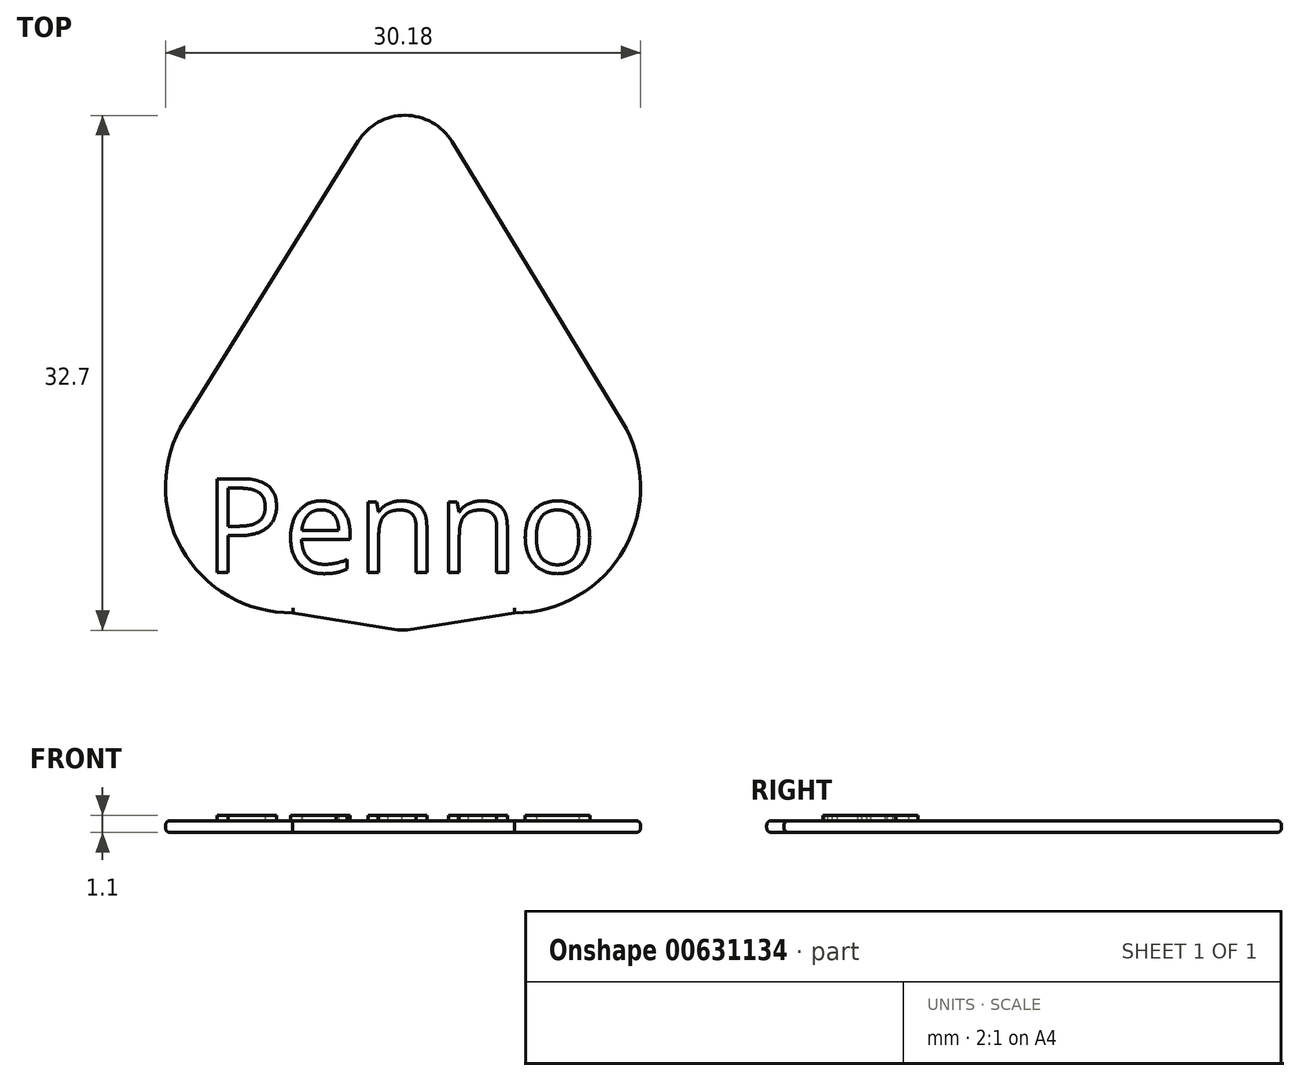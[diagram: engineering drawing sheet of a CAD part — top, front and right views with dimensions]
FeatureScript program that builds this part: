
annotation { "Feature Type Name" : "Feature", "Feature Type Description" : "" }
export const myFeature = defineFeature(function(context is Context, id is Id, definition is map)
    precondition{}
    {
        {
            var Q0;
            Q0=qCreatedBy(makeId("Top.planeOp"),FACE);
            var sketch = newSketch(context, id + "F0", { "sketchPlane" : qUnion([Q0])});
            skLineSegment(sketch, "E0", {"start": v(35.4, 12.16) * mm, "end": v(24.6, 29.92) * mm});
            skLineSegment(sketch, "E1", {"start": v(18.63, 29.95) * mm, "end": v(7.6, 12.23) * mm});
            skPoint(sketch, "E2.visualSharp", {"position": v(21.64, 34.78) * mm});
            skArc(sketch, "E2.filletArc", {"start": v(24.6, 29.92) * mm, "mid": v(21.62, 31.6) * mm, "end": v(18.63, 29.95) * mm});
            skPoint(sketch, "E3.visualSharp", {"position": v(0, 0) * mm});
            skArc(sketch, "E3.filletArc", {"start": v(7.6, 12.23) * mm, "mid": v(7.43, 4.08) * mm, "end": v(14.48, 0) * mm});
            skPoint(sketch, "E4.visualSharp", {"position": v(44.08, -2.08) * mm});
            skArc(sketch, "E4.filletArc", {"start": v(28.58, 0) * mm, "mid": v(35.55, 4.08) * mm, "end": v(35.4, 12.16) * mm});
            skLineSegment(sketch, "E5", {"start": v(7.4, -7.26) * mm, "end": v(35.4, -7.26) * mm, "construction": true});
            skPoint(sketch, "E6", {"position": v(21.47, -1.12) * mm});
            skLineSegment(sketch, "E7", {"start": v(2.06, -2.05) * mm, "end": v(2.06, 29.95) * mm, "construction": true});
            skLineSegment(sketch, "E8", {"start": v(14.48, 0) * mm, "end": v(21.15, -1.07) * mm});
            skLineSegment(sketch, "E9", {"start": v(28.58, 0) * mm, "end": v(21.78, -1.07) * mm});
            skArc(sketch, "E10.filletArc", {"start": v(21.15, -1.07) * mm, "mid": v(21.47, -1.1) * mm, "end": v(21.78, -1.07) * mm});
            skPoint(sketch, "E11", {"position": v(30, 21.04) * mm});
            skPoint(sketch, "E12", {"position": v(13.1, 21.04) * mm});
            skSolve(sketch);
        }
        {
            var Q0;
            Q0 = qSketchRegion(id + "F0", true);
            extrude(context, id + "F1", {"entities" : qUnion([Q0]), "depth" : 0.75 * mm, "offsetDistance" : 25 * mm});
        }
        {
            var Q0;
            Q0=makeQuery(id+"F1.opExtrude","CAP_EDGE",EDGE,{"disambiguationData":[OSD([sQuery(id+"F0.wireOp",EDGE,"E3.filletArc")])],"isStart":false});
            var Q1;
            Q1=makeQuery(id+"F1.opExtrude","CAP_EDGE",EDGE,{"disambiguationData":[OSD([sQuery(id+"F0.wireOp",EDGE,"E8")])],"isStart":false});
            var Q2;
            Q2=makeQuery(id+"F1.opExtrude","CAP_EDGE",EDGE,{"disambiguationData":[OSD([sQuery(id+"F0.wireOp",EDGE,"E9")])],"isStart":false});
            var Q3;
            Q3=makeQuery(id+"F1.opExtrude","CAP_EDGE",EDGE,{"disambiguationData":[OSD([sQuery(id+"F0.wireOp",EDGE,"E10.filletArc")])],"isStart":false});
            var Q4;
            Q4=makeQuery(id+"F1.opExtrude","CAP_EDGE",EDGE,{"disambiguationData":[OSD([sQuery(id+"F0.wireOp",EDGE,"E4.filletArc")])],"isStart":false});
            var Q5;
            Q5=makeQuery(id+"F1.opExtrude","CAP_EDGE",EDGE,{"disambiguationData":[OSD([sQuery(id+"F0.wireOp",EDGE,"E0")])],"isStart":false});
            var Q6;
            Q6=makeQuery(id+"F1.opExtrude","CAP_EDGE",EDGE,{"disambiguationData":[OSD([sQuery(id+"F0.wireOp",EDGE,"E1")])],"isStart":false});
            var Q7;
            Q7=makeQuery(id+"F1.opExtrude","CAP_EDGE",EDGE,{"disambiguationData":[OSD([sQuery(id+"F0.wireOp",EDGE,"E2.filletArc")])],"isStart":false});
            var Q8;
            Q8=makeQuery(id+"F1.opExtrude","CAP_EDGE",EDGE,{"disambiguationData":[OSD([sQuery(id+"F0.wireOp",EDGE,"E9")])],"isStart":true});
            var Q9;
            Q9=makeQuery(id+"F1.opExtrude","CAP_EDGE",EDGE,{"disambiguationData":[OSD([sQuery(id+"F0.wireOp",EDGE,"E4.filletArc")])],"isStart":true});
            var Q10;
            Q10=makeQuery(id+"F1.opExtrude","CAP_EDGE",EDGE,{"disambiguationData":[OSD([sQuery(id+"F0.wireOp",EDGE,"E0")])],"isStart":true});
            var Q11;
            Q11=makeQuery(id+"F1.opExtrude","CAP_EDGE",EDGE,{"disambiguationData":[OSD([sQuery(id+"F0.wireOp",EDGE,"E2.filletArc")])],"isStart":true});
            var Q12;
            Q12=makeQuery(id+"F1.opExtrude","CAP_EDGE",EDGE,{"disambiguationData":[OSD([sQuery(id+"F0.wireOp",EDGE,"E1")])],"isStart":true});
            var Q13;
            Q13=makeQuery(id+"F1.opExtrude","CAP_EDGE",EDGE,{"disambiguationData":[OSD([sQuery(id+"F0.wireOp",EDGE,"E3.filletArc")])],"isStart":true});
            var Q14;
            Q14=makeQuery(id+"F1.opExtrude","CAP_EDGE",EDGE,{"disambiguationData":[OSD([sQuery(id+"F0.wireOp",EDGE,"E8")])],"isStart":true});
            var Q15;
            Q15=makeQuery(id+"F1.opExtrude","CAP_EDGE",EDGE,{"disambiguationData":[OSD([sQuery(id+"F0.wireOp",EDGE,"E10.filletArc")])],"isStart":true});
            fillet(context, id + "F2", {"entities" : qUnion([Q0, Q1, Q2, Q3, Q4, Q5, Q6, Q7, Q8, Q9, Q10, Q11, Q12, Q13, Q14, Q15]), "radius" : 0.3 * mm, "tangentPropagation" : true, "allowEdgeOverflow" : false});
        }
        {
            var Q0;
            Q0=makeQuery(id+"F1.opExtrude","CAP_FACE",FACE,{"disambiguationData":[OSD([sQuery(id+"F0.wireOp",EDGE,"E0"),sQuery(id+"F0.wireOp",EDGE,"E1"),sQuery(id+"F0.wireOp",EDGE,"E2.filletArc"),sQuery(id+"F0.wireOp",EDGE,"E3.filletArc"),sQuery(id+"F0.wireOp",EDGE,"E4.filletArc"),sQuery(id+"F0.wireOp",EDGE,"E8"),sQuery(id+"F0.wireOp",EDGE,"E9"),sQuery(id+"F0.wireOp",EDGE,"E10.filletArc")])],"isStart":false});
            var sketch = newSketch(context, id + "F3", { "sketchPlane" : qUnion([Q0])});
            skText(sketch, "E13", { "text": "Penno", "fontName": "OpenSans-Regular.ttf"});
            const initialGuessF3  = {"E13": [0.00886, 0.00257, 1, 0, 0.006]};
            skSetInitialGuess(sketch, initialGuessF3);
            skSolve(sketch);
        }
        {
            var Q0;
            Q0 = qSketchRegion(id + "F3", true);
            extrude(context, id + "F4", {"entities" : qUnion([Q0]), "operationType" : NewBodyOperationType.ADD, "depth" : 0.35 * mm, "offsetDistance" : 25 * mm});
        }
    });
